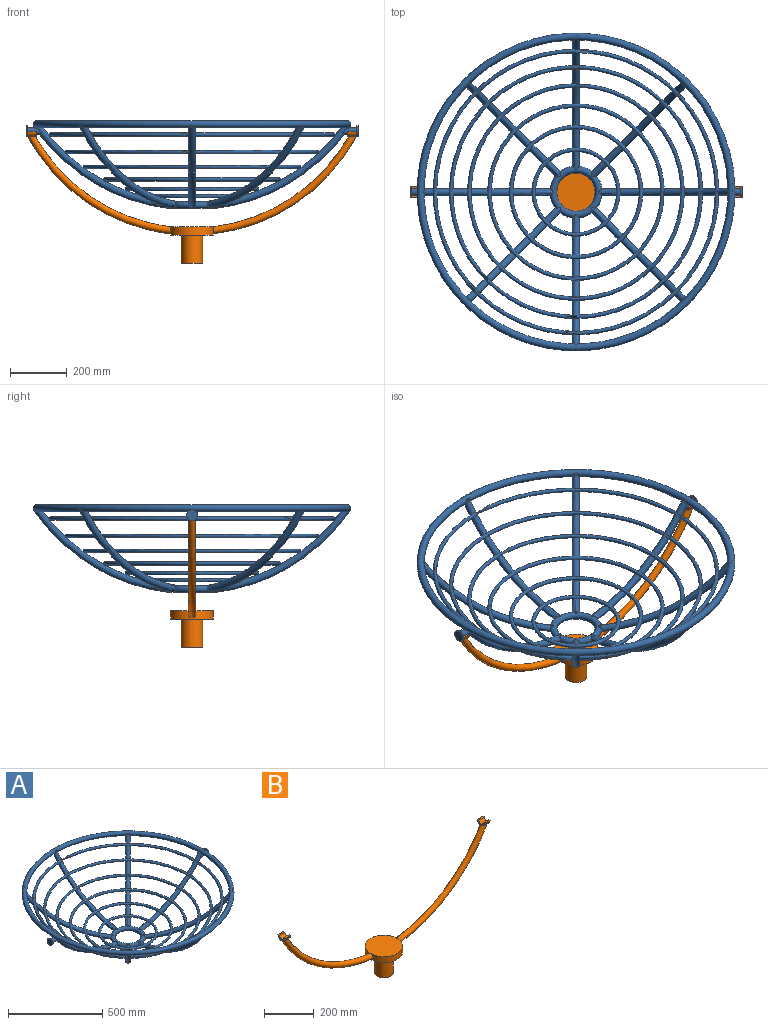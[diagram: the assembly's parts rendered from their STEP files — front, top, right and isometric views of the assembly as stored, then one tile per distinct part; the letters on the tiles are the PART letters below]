
ASSEMBLY  parts=2 mates=1
PART A: 121 faces, bbox 1217.7x1217.7x360.8 mm
  f0: cylinder r=12.5mm len=50.41mm, axis (-1,0,0), area 3188.7mm2, adj f3,f38
  f1: torus R=665.68mm, axis (0,-1,0), area 42408mm2, adj f2,f10,f11,f12,f13,f14,f15,f16
  f2: torus R=550mm, axis (0,0,-1), area 266434.7mm2, adj f1,f3,f4,f5,f6,f7,f8,f9
  f3: torus R=665.68mm, axis (0,1,0), area 42405.8mm2, adj f0,f2,f10,f11,f12,f13,f14,f15
  f4: torus R=665.68mm, axis (-0.71,0.71,0), area 43182.2mm2, adj f2,f10,f11,f12,f13,f14,f15,f16
  f5: torus R=665.68mm, axis (-1,0,0), area 43183.6mm2, adj f2,f10,f11,f12,f13,f14,f15,f16
  f6: torus R=665.68mm, axis (-0.71,-0.71,0), area 43182.9mm2, adj f2,f10,f11,f12,f13,f14,f15,f16
  f7: torus R=665.68mm, axis (0.71,-0.71,0), area 43185.4mm2, adj f2,f10,f11,f12,f13,f14,f15,f16
  f8: torus R=665.68mm, axis (1,0,0), area 43180.7mm2, adj f2,f10,f11,f12,f13,f14,f15,f16
  f9: torus R=665.68mm, axis (0.71,0.71,0), area 43183.6mm2, adj f2,f10,f11,f12,f13,f14,f15,f16
  f10: torus R=499.25mm, axis (0,0,-1), area 124962.6mm2, adj f1,f3,f4,f5,f6,f7,f8,f9
  f11: torus R=441.91mm, axis (0,0,-1), area 110597.4mm2, adj f1,f3,f4,f5,f6,f7,f8,f9
  f12: torus R=377.19mm, axis (0,0,-1), area 94366.2mm2, adj f1,f3,f4,f5,f6,f7,f8,f9
  f13: torus R=306.15mm, axis (0,0,-1), area 76565.1mm2, adj f1,f3,f4,f5,f6,f7,f8,f9
  f14: torus R=230mm, axis (0,0,-1), area 57472.1mm2, adj f1,f3,f4,f5,f6,f7,f8,f9
  f15: torus R=150mm, axis (0,0,-1), area 37413.5mm2, adj f1,f3,f4,f5,f6,f7,f8,f9
  f16: torus R=80mm, axis (0,0,-1), area 34484.5mm2, adj f1,f3,f4,f5,f6,f7,f8,f9
  f17: torus R=665.68mm, axis (0.71,0.71,0), area 0mm2, adj f16
  f18: torus R=665.68mm, axis (1,0,0), area 0mm2, adj f16
  f19: torus R=665.68mm, axis (0.71,-0.71,0), area 0mm2, adj f16
  f20: torus R=665.68mm, axis (0.71,-0.71,0), area 0mm2, adj f16
  f21: torus R=665.68mm, axis (0,-1,0), area 0mm2, adj f16
  f22: torus R=665.68mm, axis (-0.71,-0.71,0), area 0mm2, adj f16
  f23: torus R=665.68mm, axis (-0.71,-0.71,0), area 0mm2, adj f16
  f24: torus R=665.68mm, axis (-1,0,0), area 0mm2, adj f16
  f25: torus R=665.68mm, axis (-0.71,0.71,0), area 0mm2, adj f16
  f26: torus R=665.68mm, axis (-0.71,0.71,0), area 0mm2, adj f16
  f27: torus R=665.68mm, axis (0,1,0), area 0mm2, adj f16
  f28: torus R=665.68mm, axis (1,0,0), area 0mm2, adj f16
  f29: torus R=665.68mm, axis (0,-1,0), area 0mm2, adj f16
  f30: torus R=665.68mm, axis (-1,0,0), area 0mm2, adj f16
  f31: torus R=665.68mm, axis (0,1,0), area 0mm2, adj f16
  f32: torus R=665.68mm, axis (0.71,0.71,0), area 0mm2, adj f16
  f33: cylinder r=12.5mm len=50.41mm, axis (1,0,0), area 3188.7mm2, adj f1,f35
  f34: cylinder r=20mm len=40mm, axis (1,0,0), area 628.3mm2, adj f35,f36
  f35: plane 40x40mm, normal (-1,0,0), area 765.8mm2, adj f33,f34
  f36: plane 40x40mm, normal (1,0,0), area 1256.6mm2, adj f34
  f37: cylinder r=20mm len=40mm, axis (-1,0,0), area 628.3mm2, adj f38,f39
  f38: plane 40x40mm, normal (1,0,0), area 765.8mm2, adj f0,f37
  f39: plane 40x40mm, normal (-1,0,0), area 1256.6mm2, adj f37
  f40: torus R=80mm, axis (0,0,-1), area 348.4mm2, adj f41
  f41: torus R=665.68mm, axis (0,1,0), area 34367.1mm2, adj f40,f42
  f42: torus R=550mm, axis (0,0,-1), area 349mm2, adj f41
  f43: torus R=80mm, axis (0,0,-1), area 349.2mm2, adj f44
  f44: torus R=665.68mm, axis (-0.71,0.71,0), area 34366mm2, adj f43,f45
  f45: torus R=550mm, axis (0,0,-1), area 348.7mm2, adj f44
  f46: torus R=80mm, axis (0,0,-1), area 348.1mm2, adj f47
  f47: torus R=665.68mm, axis (-1,0,0), area 34362.3mm2, adj f46,f48
  f48: torus R=550mm, axis (0,0,-1), area 348.6mm2, adj f47
  f49: torus R=80mm, axis (0,0,-1), area 349.3mm2, adj f50
  f50: torus R=665.68mm, axis (-0.71,-0.71,0), area 34370.3mm2, adj f49,f51
  f51: torus R=550mm, axis (0,0,-1), area 348.4mm2, adj f50
  f52: torus R=80mm, axis (0,0,-1), area 349mm2, adj f53
  f53: torus R=665.68mm, axis (0,-1,0), area 34366.6mm2, adj f52,f54
  f54: torus R=550mm, axis (0,0,-1), area 348.8mm2, adj f53
  f55: torus R=80mm, axis (0,0,-1), area 349mm2, adj f56
  f56: torus R=665.68mm, axis (0.71,-0.71,0), area 34372.7mm2, adj f55,f57
  f57: torus R=550mm, axis (0,0,-1), area 348.8mm2, adj f56
  f58: torus R=80mm, axis (0,0,-1), area 349.6mm2, adj f59
  f59: torus R=665.68mm, axis (1,0,0), area 34375.1mm2, adj f58,f60
  f60: torus R=550mm, axis (0,0,-1), area 348.8mm2, adj f59
  f61: torus R=80mm, axis (0,0,-1), area 349.3mm2, adj f62
  f62: torus R=665.68mm, axis (0.71,0.71,0), area 34367.4mm2, adj f61,f63
  f63: torus R=550mm, axis (0,0,-1), area 348.4mm2, adj f62
  f64: torus R=550mm, axis (0,0,-1), area 400.1mm2, adj f66,f69
  f65: plane 16.58x12.52mm, normal (-0.56,0,0.83), area 62.8mm2, adj f66,f67,f71
  f66: torus R=665.68mm, axis (0,1,0), area 200.8mm2, adj f64,f65
  f67: torus R=665.68mm, axis (0,1,0), area 175.8mm2, adj f65,f71
  f68: plane 16.58x12.52mm, normal (-0.56,0,0.83), area 62.8mm2, adj f69,f70,f71
  f69: torus R=665.68mm, axis (0,1,0), area 200.8mm2, adj f64,f68
  f70: torus R=665.68mm, axis (0,1,0), area 175.8mm2, adj f68,f71
  f71: torus R=550mm, axis (0,0,-1), area 212009.2mm2, adj f65,f67,f68,f70,f72,f74,f75,f77
  f72: plane 17.32x17.32mm, normal (-0.4,0.4,0.83), area 62.8mm2, adj f71,f73,f74
  f73: torus R=665.68mm, axis (0.71,0.71,0), area 200.8mm2, adj f72,f111
  f74: torus R=665.68mm, axis (0.71,0.71,0), area 175.8mm2, adj f71,f72
  f75: plane 16.58x12.52mm, normal (0,0.56,0.83), area 62.8mm2, adj f71,f76,f77
  f76: torus R=665.68mm, axis (1,0,0), area 200.8mm2, adj f75,f112
  f77: torus R=665.68mm, axis (1,0,0), area 175.8mm2, adj f71,f75
  f78: plane 16.58x12.52mm, normal (0,0.56,0.83), area 62.8mm2, adj f71,f79,f80
  f79: torus R=665.68mm, axis (1,0,0), area 200.8mm2, adj f78,f112
  f80: torus R=665.68mm, axis (1,0,0), area 175.8mm2, adj f71,f78
  f81: plane 17.32x17.32mm, normal (0.4,0.4,0.83), area 62.8mm2, adj f71,f82,f83
  f82: torus R=665.68mm, axis (0.71,-0.71,0), area 200.8mm2, adj f81,f113
  f83: torus R=665.68mm, axis (0.71,-0.71,0), area 175.8mm2, adj f71,f81
  f84: plane 17.32x17.32mm, normal (0.4,0.4,0.83), area 62.8mm2, adj f71,f85,f86
  f85: torus R=665.68mm, axis (0.71,-0.71,0), area 200.8mm2, adj f84,f113
  f86: torus R=665.68mm, axis (0.71,-0.71,0), area 175.8mm2, adj f71,f84
  f87: plane 16.58x12.52mm, normal (0.56,0,0.83), area 62.8mm2, adj f71,f88,f89
  f88: torus R=665.68mm, axis (0,-1,0), area 200.8mm2, adj f87,f114
  f89: torus R=665.68mm, axis (0,-1,0), area 175.8mm2, adj f71,f87
  f90: plane 16.58x12.52mm, normal (0.56,0,0.83), area 62.8mm2, adj f71,f91,f92
  f91: torus R=665.68mm, axis (0,-1,0), area 200.8mm2, adj f90,f114
  f92: torus R=665.68mm, axis (0,-1,0), area 175.8mm2, adj f71,f90
  f93: plane 17.32x17.32mm, normal (0.4,-0.4,0.83), area 62.8mm2, adj f71,f94,f95
  f94: torus R=665.68mm, axis (-0.71,-0.71,0), area 200.8mm2, adj f93,f115
  f95: torus R=665.68mm, axis (-0.71,-0.71,0), area 175.8mm2, adj f71,f93
  f96: plane 17.32x17.32mm, normal (0.4,-0.4,0.83), area 62.8mm2, adj f71,f97,f98
  f97: torus R=665.68mm, axis (-0.71,-0.71,0), area 200.8mm2, adj f96,f115
  f98: torus R=665.68mm, axis (-0.71,-0.71,0), area 175.8mm2, adj f71,f96
  f99: plane 16.58x12.52mm, normal (0,-0.56,0.83), area 62.8mm2, adj f71,f100,f101
  f100: torus R=665.68mm, axis (-1,0,0), area 200.8mm2, adj f99,f116
  f101: torus R=665.68mm, axis (-1,0,0), area 175.8mm2, adj f71,f99
  f102: plane 16.58x12.52mm, normal (0,-0.56,0.83), area 62.8mm2, adj f71,f103,f104
  f103: torus R=665.68mm, axis (-1,0,0), area 200.8mm2, adj f102,f116
  f104: torus R=665.68mm, axis (-1,0,0), area 175.8mm2, adj f71,f102
  f105: plane 17.32x17.32mm, normal (-0.4,-0.4,0.83), area 62.8mm2, adj f71,f106,f107
  f106: torus R=665.68mm, axis (-0.71,0.71,0), area 200.8mm2, adj f105,f117
  f107: torus R=665.68mm, axis (-0.71,0.71,0), area 175.8mm2, adj f71,f105
  f108: plane 17.32x17.32mm, normal (-0.4,-0.4,0.83), area 62.8mm2, adj f71,f109,f110
  f109: torus R=665.68mm, axis (-0.71,0.71,0), area 200.8mm2, adj f108,f117
  f110: torus R=665.68mm, axis (-0.71,0.71,0), area 175.8mm2, adj f71,f108
  f111: torus R=550mm, axis (0,0,-1), area 400.1mm2, adj f73,f119
  f112: torus R=550mm, axis (0,0,-1), area 400.1mm2, adj f76,f79
  f113: torus R=550mm, axis (0,0,-1), area 400.1mm2, adj f82,f85
  f114: torus R=550mm, axis (0,0,-1), area 400.1mm2, adj f88,f91
  f115: torus R=550mm, axis (0,0,-1), area 400.1mm2, adj f94,f97
  f116: torus R=550mm, axis (0,0,-1), area 400.1mm2, adj f100,f103
  f117: torus R=550mm, axis (0,0,-1), area 400.1mm2, adj f106,f109
  f118: plane 17.32x17.32mm, normal (-0.4,0.4,0.83), area 62.8mm2, adj f71,f119,f120
  f119: torus R=665.68mm, axis (0.71,0.71,0), area 200.8mm2, adj f111,f118
  f120: torus R=665.68mm, axis (0.71,0.71,0), area 175.8mm2, adj f71,f118
PART B: 27 faces, bbox 1258.2x150x467.5 mm
  f0: torus R=647mm, axis (0,-1,0), area 48571.7mm2, adj f4,f8
  f1: plane 40x20mm, normal (-1,0,0), area 382.9mm2, adj f3,f4,f5,f6
  f2: plane 40x20mm, normal (1,0,0), area 382.9mm2, adj f3,f4,f5,f6
  f3: plane 31.5x7.5mm, normal (0,0,1), area 236.2mm2, adj f1,f2,f4,f6
  f4: cylinder r=20mm len=40mm, axis (-1,0,0), area 1386.7mm2, adj f0,f1,f2,f3,f5
  f5: plane 31.5x7.5mm, normal (0,0,1), area 236.2mm2, adj f1,f2,f4,f6
  f6: cylinder r=12.5mm len=31.5mm, axis (-1,0,0), area 1237mm2, adj f1,f2,f3,f5
  f7: plane 150x150mm, normal (0,0,-1), area 13111.1mm2, adj f8,f18
  f8: cylinder r=75mm len=150mm, axis (0,0,1), area 13148.3mm2, adj f0,f7,f9,f16
  f9: plane 150x150mm, normal (0,0,1), area 17671.5mm2, adj f8
  f10: cylinder r=12.5mm len=31.5mm, axis (1,0,0), area 1237mm2, adj f11,f12,f13,f14
  f11: plane 31.5x7.5mm, normal (0,0,1), area 236.2mm2, adj f10,f12,f14,f15
  f12: plane 40x20mm, normal (-1,0,0), area 382.9mm2, adj f10,f11,f13,f15
  f13: plane 31.5x7.5mm, normal (0,0,1), area 236.2mm2, adj f10,f12,f14,f15
  f14: plane 40x20mm, normal (1,0,0), area 382.9mm2, adj f10,f11,f13,f15
  f15: cylinder r=20mm len=40mm, axis (1,0,0), area 1387.2mm2, adj f11,f12,f13,f14,f16
  f16: torus R=647mm, axis (0,-1,0), area 48574.8mm2, adj f8,f15
  f17: cylinder r=35mm len=100mm, axis (0,0,1), area 21991.1mm2, adj f19,f20
  f18: cylinder r=38.1mm len=100mm, axis (0,0,1), area 23938.9mm2, adj f7,f19
  f19: plane 76.2x76.2mm, normal (0,0,-1), area 711.9mm2, adj f17,f18
  f20: plane 70x70mm, normal (0,0,-1), area 3848.5mm2, adj f17
  f21: cylinder r=20mm len=22.83mm, axis (1,0,0), area 370.9mm2, adj f22
  f22: torus R=647mm, axis (0,-1,0), area 38793.5mm2, adj f21,f23
  f23: cylinder r=75mm len=20.14mm, axis (0,0,1), area 316.9mm2, adj f22
  f24: torus R=647mm, axis (0,-1,0), area 38787.6mm2, adj f25,f26
  f25: cylinder r=20mm len=22.83mm, axis (-1,0,0), area 370.8mm2, adj f24
  f26: cylinder r=75mm len=20.14mm, axis (0,0,1), area 317mm2, adj f24
PLACE A t=(44.99,59.82,59.51)mm
PLACE B t=(44.99,59.82,59.51)mm
MATE revolute A.f0 <-> B.f4  axis (1,0,0) through (627.49,59.82,34.51)mm
